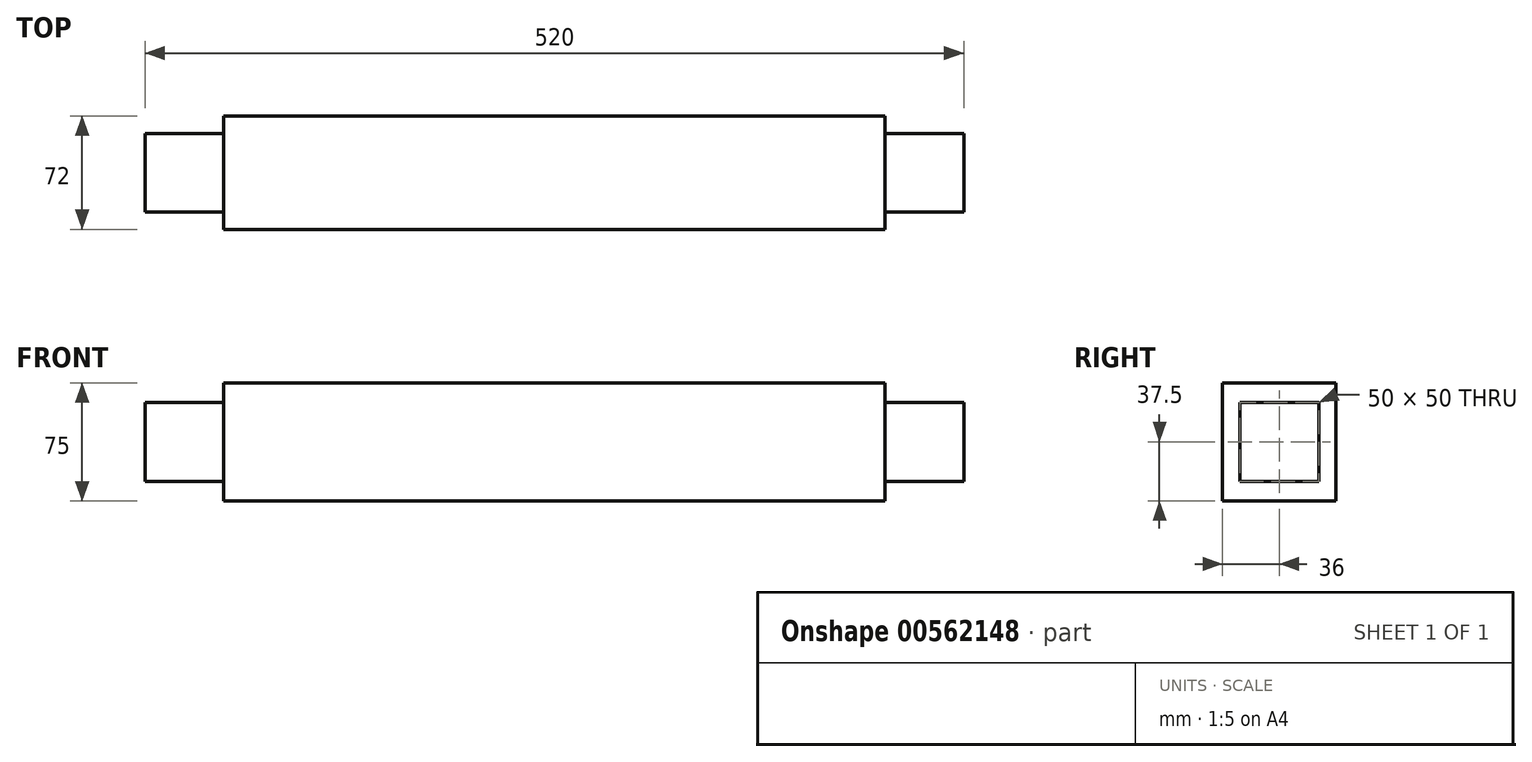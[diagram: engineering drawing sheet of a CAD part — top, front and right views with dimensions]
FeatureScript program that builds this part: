
annotation { "Feature Type Name" : "Feature", "Feature Type Description" : "" }
export const myFeature = defineFeature(function(context is Context, id is Id, definition is map)
    precondition{}
    {
        {
            var Q0;
            Q0=qCreatedBy(makeId("Front.planeOp"),FACE);
            var sketch = newSketch(context, id + "F0", { "sketchPlane" : qUnion([Q0])});
            skLineSegment(sketch, "E0.bottom", {"start": v(210, 37.5) * mm, "end": v(-210, 37.5) * mm});
            skLineSegment(sketch, "E0.top", {"start": v(210, -37.5) * mm, "end": v(-210, -37.5) * mm});
            skLineSegment(sketch, "E0.left", {"start": v(210, 37.5) * mm, "end": v(210, -37.5) * mm});
            skLineSegment(sketch, "E0.right", {"start": v(-210, 37.5) * mm, "end": v(-210, -37.5) * mm});
            skPoint(sketch, "E0.middle", {"position": v(0, 0) * mm});
            skSolve(sketch);
        }
        {
            var Q0;
            Q0 = qSketchRegion(id + "F0", true);
            extrude(context, id + "F1", {"entities" : qUnion([Q0]), "depth" : 72 * mm, "offsetDistance" : 25 * mm});
        }
        {
            var Q0;
            Q0=makeQuery(id+"F1.opExtrude","SWEPT_FACE",FACE,{"disambiguationData":[OSD([sQuery(id+"F0.wireOp",EDGE,"E0.left")])]});
            var sketch = newSketch(context, id + "F2", { "sketchPlane" : qUnion([Q0])});
            skLineSegment(sketch, "E1.bottom", {"start": v(-61, -25) * mm, "end": v(-11, -25) * mm});
            skLineSegment(sketch, "E1.top", {"start": v(-61, 25) * mm, "end": v(-11, 25) * mm});
            skLineSegment(sketch, "E1.left", {"start": v(-61, -25) * mm, "end": v(-61, 25) * mm});
            skLineSegment(sketch, "E1.right", {"start": v(-11, -25) * mm, "end": v(-11, 25) * mm});
            skPoint(sketch, "E1.middle", {"position": v(-36, 0) * mm});
            skPoint(sketch, "E1.middle.positionSnap0", {"position": v(-36, 37.5) * mm});
            skPoint(sketch, "E1.centerSnap0", {"position": v(-36, 37.5) * mm});
            skSolve(sketch);
        }
        {
            var Q0;
            Q0=makeQuery(id+"F2.imprint","IMPRINT",FACE,{"disambiguationData":[TD([[makeQuery(id+"F2.imprint","IMPRINT",EDGE,{"derivedFrom":sQuery(id+"F2.wireOp",EDGE,"E1.bottom")}),1.0]])]});
            extrude(context, id + "F3", {"entities" : qUnion([Q0]), "operationType" : NewBodyOperationType.ADD, "depth" : 50 * mm, "offsetDistance" : 25 * mm});
        }
        {
            var Q0;
            Q0=makeQuery(id+"F1.opExtrude","SWEPT_FACE",FACE,{"disambiguationData":[OSD([sQuery(id+"F0.wireOp",EDGE,"E0.right")])]});
            var sketch = newSketch(context, id + "F4", { "sketchPlane" : qUnion([Q0])});
            skLineSegment(sketch, "E2.bottom", {"start": v(11, -25) * mm, "end": v(61, -25) * mm});
            skLineSegment(sketch, "E2.top", {"start": v(11, 25) * mm, "end": v(61, 25) * mm});
            skLineSegment(sketch, "E2.left", {"start": v(11, -25) * mm, "end": v(11, 25) * mm});
            skLineSegment(sketch, "E2.right", {"start": v(61, -25) * mm, "end": v(61, 25) * mm});
            skPoint(sketch, "E2.middle", {"position": v(36, 0) * mm});
            skPoint(sketch, "E2.middle.positionSnap0", {"position": v(72, 0) * mm});
            skPoint(sketch, "E2.middle.positionSnap1", {"position": v(36, 37.5) * mm});
            skPoint(sketch, "E2.centerSnap0", {"position": v(72, 0) * mm});
            skPoint(sketch, "E2.centerSnap1", {"position": v(36, 37.5) * mm});
            skSolve(sketch);
        }
        {
            var Q0;
            Q0 = qSketchRegion(id + "F4", true);
            extrude(context, id + "F5", {"entities" : qUnion([Q0]), "operationType" : NewBodyOperationType.ADD, "depth" : 50 * mm, "offsetDistance" : 25 * mm});
        }
    });
